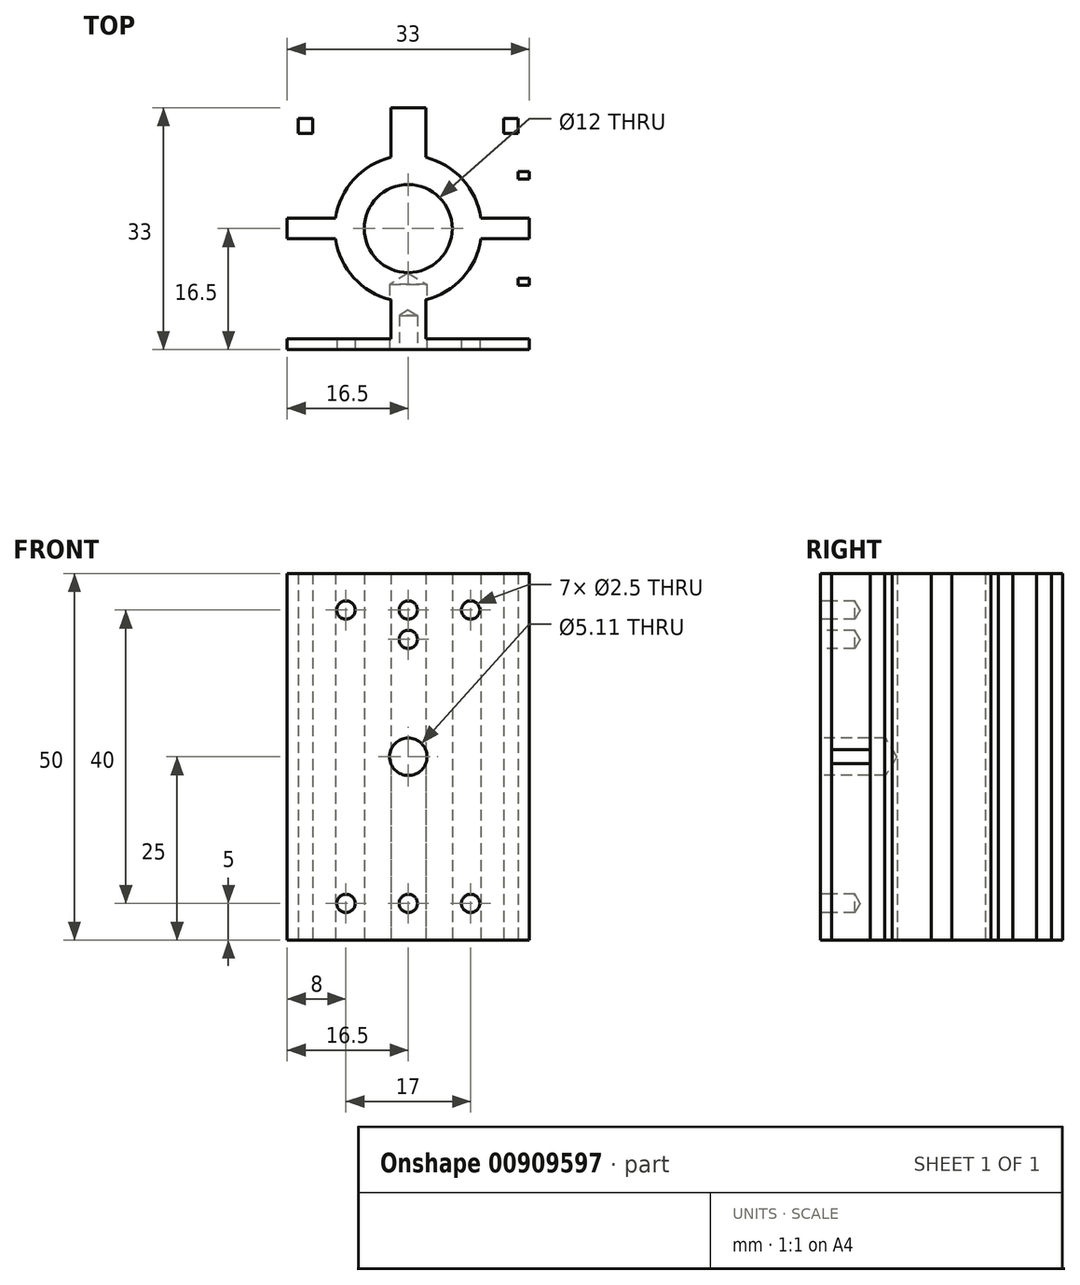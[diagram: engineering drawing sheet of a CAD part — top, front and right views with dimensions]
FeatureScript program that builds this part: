
annotation { "Feature Type Name" : "Feature", "Feature Type Description" : "" }
export const myFeature = defineFeature(function(context is Context, id is Id, definition is map)
    precondition{}
    {
        {
            var Q0;
            Q0=qCreatedBy(makeId("Top.planeOp"),FACE);
            var sketch = newSketch(context, id + "F0", { "sketchPlane" : qUnion([Q0])});
            skLineSegment(sketch, "E0.bottom", {"start": v(16.5, 16.5) * mm, "end": v(-16.5, 16.5) * mm});
            skLineSegment(sketch, "E0.top", {"start": v(16.5, -16.5) * mm, "end": v(-16.5, -16.5) * mm});
            skLineSegment(sketch, "E0.left", {"start": v(16.5, 16.5) * mm, "end": v(16.5, -16.5) * mm});
            skLineSegment(sketch, "E0.right", {"start": v(-16.5, 16.5) * mm, "end": v(-16.5, -16.5) * mm});
            skPoint(sketch, "E0.middle", {"position": v(0, 0) * mm});
            skCircle(sketch, "E1", {"center": v(0, 0) * mm, "radius": 10 * mm});
            skLineSegment(sketch, "E2", {"start": v(0, 16.5) * mm, "end": v(0, -16.5) * mm, "construction": true});
            skLineSegment(sketch, "E3", {"start": v(-16.5, 0) * mm, "end": v(16.5, 0) * mm, "construction": true});
            skLineSegment(sketch, "E4", {"start": v(-2.38, 9.71) * mm, "end": v(-2.38, 16.5) * mm});
            skLineSegment(sketch, "E5.MirrorCS", {"start": v(2.38, 9.71) * mm, "end": v(2.38, 16.5) * mm});
            skLineSegment(sketch, "E6.MirrorCS", {"start": v(-2.38, -9.71) * mm, "end": v(-2.38, -16.5) * mm});
            skLineSegment(sketch, "E7.MirrorCS", {"start": v(2.37, -9.71) * mm, "end": v(2.37, -16.5) * mm});
            skLineSegment(sketch, "E8", {"start": v(-16.5, -1.4) * mm, "end": v(-9.9, -1.4) * mm});
            skLineSegment(sketch, "E9.MirrorCS", {"start": v(-16.5, 1.4) * mm, "end": v(-9.9, 1.4) * mm});
            skLineSegment(sketch, "E10.MirrorCS", {"start": v(16.5, 1.4) * mm, "end": v(9.9, 1.4) * mm});
            skLineSegment(sketch, "E11.MirrorCS", {"start": v(16.5, -1.4) * mm, "end": v(9.9, -1.4) * mm});
            skLineSegment(sketch, "E12.0", {"start": v(13, 13) * mm, "end": v(13, -13) * mm});
            skLineSegment(sketch, "E12.1", {"start": v(13, 13) * mm, "end": v(-13, 13) * mm});
            skLineSegment(sketch, "E12.2", {"start": v(-13, 13) * mm, "end": v(-13, -13) * mm});
            skLineSegment(sketch, "E12.3", {"start": v(13, -13) * mm, "end": v(-13, -13) * mm});
            skLineSegment(sketch, "E13.0", {"start": v(15, 15) * mm, "end": v(-15, 15) * mm});
            skLineSegment(sketch, "E13.1", {"start": v(15, 15) * mm, "end": v(15, -15) * mm});
            skLineSegment(sketch, "E13.2", {"start": v(15, -15) * mm, "end": v(-15, -15) * mm});
            skLineSegment(sketch, "E13.3", {"start": v(-15, 15) * mm, "end": v(-15, -15) * mm});
            skLineSegment(sketch, "E14.bottom", {"start": v(-10.5, 16.5) * mm, "end": v(-9.5, 16.5) * mm});
            skLineSegment(sketch, "E14.top", {"start": v(-10.5, 15) * mm, "end": v(-9.5, 15) * mm});
            skLineSegment(sketch, "E14.left", {"start": v(-10.5, 16.5) * mm, "end": v(-10.5, 15) * mm});
            skLineSegment(sketch, "E14.right", {"start": v(-9.5, 16.5) * mm, "end": v(-9.5, 15) * mm});
            skLineSegment(sketch, "E15.bottom", {"start": v(-16.5, 16.5) * mm, "end": v(-13, 16.5) * mm});
            skLineSegment(sketch, "E15.top", {"start": v(-16.5, 13) * mm, "end": v(-13, 13) * mm});
            skLineSegment(sketch, "E15.left", {"start": v(-16.5, 16.5) * mm, "end": v(-16.5, 13) * mm});
            skLineSegment(sketch, "E15.right", {"start": v(-13, 16.5) * mm, "end": v(-13, 13) * mm});
            skLineSegment(sketch, "E16.1.0.0", {"start": v(-7.75, 16.5) * mm, "end": v(-6.75, 16.5) * mm});
            skLineSegment(sketch, "E16.1.0.1", {"start": v(-7.75, 15) * mm, "end": v(-6.75, 15) * mm});
            skLineSegment(sketch, "E16.1.0.2", {"start": v(-7.75, 16.5) * mm, "end": v(-7.75, 15) * mm});
            skLineSegment(sketch, "E16.1.0.3", {"start": v(-6.75, 16.5) * mm, "end": v(-6.75, 15) * mm});
            skLineSegment(sketch, "E16.2.0.0", {"start": v(-5, 16.5) * mm, "end": v(-4, 16.5) * mm});
            skLineSegment(sketch, "E16.2.0.1", {"start": v(-5, 15) * mm, "end": v(-4, 15) * mm});
            skLineSegment(sketch, "E16.2.0.2", {"start": v(-5, 16.5) * mm, "end": v(-5, 15) * mm});
            skLineSegment(sketch, "E16.2.0.3", {"start": v(-4, 16.5) * mm, "end": v(-4, 15) * mm});
            skLineSegment(sketch, "E16.direction1", {"start": v(-10.5, 15) * mm, "end": v(-7.75, 15) * mm, "construction": true});
            skLineSegment(sketch, "E17.MirrorCS", {"start": v(7.75, 16.5) * mm, "end": v(6.75, 16.5) * mm});
            skLineSegment(sketch, "E18.MirrorCS", {"start": v(7.75, 15) * mm, "end": v(6.75, 15) * mm});
            skLineSegment(sketch, "E19.MirrorCS", {"start": v(10.5, 15) * mm, "end": v(9.5, 15) * mm});
            skLineSegment(sketch, "E20.MirrorCS", {"start": v(7.75, 16.5) * mm, "end": v(7.75, 15) * mm});
            skLineSegment(sketch, "E21.MirrorCS", {"start": v(5, 15) * mm, "end": v(4, 15) * mm});
            skLineSegment(sketch, "E22.MirrorCS", {"start": v(10.5, 16.5) * mm, "end": v(10.5, 15) * mm});
            skLineSegment(sketch, "E23.MirrorCS", {"start": v(4, 16.5) * mm, "end": v(4, 15) * mm});
            skLineSegment(sketch, "E24.MirrorCS", {"start": v(10.5, 16.5) * mm, "end": v(9.5, 16.5) * mm});
            skLineSegment(sketch, "E25.MirrorCS", {"start": v(9.5, 16.5) * mm, "end": v(9.5, 15) * mm});
            skLineSegment(sketch, "E26.MirrorCS", {"start": v(5, 16.5) * mm, "end": v(5, 15) * mm});
            skLineSegment(sketch, "E27.MirrorCS", {"start": v(10.5, 15) * mm, "end": v(7.75, 15) * mm, "construction": true});
            skLineSegment(sketch, "E28.MirrorCS", {"start": v(5, 16.5) * mm, "end": v(4, 16.5) * mm});
            skLineSegment(sketch, "E29.MirrorCS", {"start": v(6.75, 16.5) * mm, "end": v(6.75, 15) * mm});
            skLineSegment(sketch, "E30", {"start": v(16.5, 16.5) * mm, "end": v(-16.5, -16.5) * mm, "construction": true});
            skLineSegment(sketch, "E31.MirrorCS", {"start": v(15, 10.5) * mm, "end": v(15, 9.5) * mm});
            skLineSegment(sketch, "E32.MirrorCS", {"start": v(16.5, 10.5) * mm, "end": v(16.5, 9.5) * mm});
            skLineSegment(sketch, "E33.MirrorCS", {"start": v(16.5, 7.75) * mm, "end": v(15, 7.75) * mm});
            skLineSegment(sketch, "E34.MirrorCS", {"start": v(15, 5) * mm, "end": v(15, 4) * mm});
            skLineSegment(sketch, "E35.MirrorCS", {"start": v(16.5, 4) * mm, "end": v(15, 4) * mm});
            skLineSegment(sketch, "E36.MirrorCS", {"start": v(16.5, 6.75) * mm, "end": v(15, 6.75) * mm});
            skLineSegment(sketch, "E37.MirrorCS", {"start": v(16.5, 7.75) * mm, "end": v(16.5, 6.75) * mm});
            skLineSegment(sketch, "E38.MirrorCS", {"start": v(16.5, 10.5) * mm, "end": v(15, 10.5) * mm});
            skLineSegment(sketch, "E39.MirrorCS", {"start": v(16.5, 5) * mm, "end": v(15, 5) * mm});
            skLineSegment(sketch, "E40.MirrorCS", {"start": v(15, 10.5) * mm, "end": v(15, 7.75) * mm, "construction": true});
            skLineSegment(sketch, "E41.MirrorCS", {"start": v(16.5, 9.5) * mm, "end": v(15, 9.5) * mm});
            skLineSegment(sketch, "E42.MirrorCS", {"start": v(15, 7.75) * mm, "end": v(15, 6.75) * mm});
            skLineSegment(sketch, "E43.MirrorCS", {"start": v(16.5, 5) * mm, "end": v(16.5, 4) * mm});
            skLineSegment(sketch, "E44.MirrorCS", {"start": v(15, -10.5) * mm, "end": v(15, -9.5) * mm});
            skLineSegment(sketch, "E45.MirrorCS", {"start": v(16.5, -7.75) * mm, "end": v(15, -7.75) * mm});
            skLineSegment(sketch, "E46.MirrorCS", {"start": v(16.5, -6.75) * mm, "end": v(15, -6.75) * mm});
            skLineSegment(sketch, "E47.MirrorCS", {"start": v(15, -5) * mm, "end": v(15, -4) * mm});
            skLineSegment(sketch, "E48.MirrorCS", {"start": v(15, -10.5) * mm, "end": v(15, -7.75) * mm, "construction": true});
            skLineSegment(sketch, "E49.MirrorCS", {"start": v(15, -7.75) * mm, "end": v(15, -6.75) * mm});
            skLineSegment(sketch, "E50.MirrorCS", {"start": v(16.5, -7.75) * mm, "end": v(16.5, -6.75) * mm});
            skLineSegment(sketch, "E51.MirrorCS", {"start": v(16.5, -9.5) * mm, "end": v(15, -9.5) * mm});
            skLineSegment(sketch, "E52.MirrorCS", {"start": v(16.5, -5) * mm, "end": v(16.5, -4) * mm});
            skLineSegment(sketch, "E53.MirrorCS", {"start": v(16.5, -4) * mm, "end": v(15, -4) * mm});
            skLineSegment(sketch, "E54.MirrorCS", {"start": v(16.5, -5) * mm, "end": v(15, -5) * mm});
            skLineSegment(sketch, "E55.MirrorCS", {"start": v(16.5, -10.5) * mm, "end": v(16.5, -9.5) * mm});
            skLineSegment(sketch, "E56.MirrorCS", {"start": v(16.5, -10.5) * mm, "end": v(15, -10.5) * mm});
            skLineSegment(sketch, "E57.MirrorCS", {"start": v(-15, 10.5) * mm, "end": v(-15, 9.5) * mm});
            skLineSegment(sketch, "E58.MirrorCS", {"start": v(-15, 7.75) * mm, "end": v(-15, 6.75) * mm});
            skLineSegment(sketch, "E59.MirrorCS", {"start": v(-16.5, 5) * mm, "end": v(-16.5, 4) * mm});
            skLineSegment(sketch, "E60.MirrorCS", {"start": v(-16.5, 4) * mm, "end": v(-15, 4) * mm});
            skLineSegment(sketch, "E61.MirrorCS", {"start": v(-16.5, 7.75) * mm, "end": v(-16.5, 6.75) * mm});
            skLineSegment(sketch, "E62.MirrorCS", {"start": v(-16.5, 5) * mm, "end": v(-15, 5) * mm});
            skLineSegment(sketch, "E63.MirrorCS", {"start": v(-16.5, 9.5) * mm, "end": v(-15, 9.5) * mm});
            skLineSegment(sketch, "E64.MirrorCS", {"start": v(-16.5, 10.5) * mm, "end": v(-16.5, 9.5) * mm});
            skLineSegment(sketch, "E65.MirrorCS", {"start": v(-16.5, 6.75) * mm, "end": v(-15, 6.75) * mm});
            skLineSegment(sketch, "E66.MirrorCS", {"start": v(-16.5, 10.5) * mm, "end": v(-15, 10.5) * mm});
            skLineSegment(sketch, "E67.MirrorCS", {"start": v(-15, 5) * mm, "end": v(-15, 4) * mm});
            skLineSegment(sketch, "E68.MirrorCS", {"start": v(-16.5, 7.75) * mm, "end": v(-15, 7.75) * mm});
            skLineSegment(sketch, "E69.MirrorCS", {"start": v(-15, 10.5) * mm, "end": v(-15, 7.75) * mm, "construction": true});
            skLineSegment(sketch, "E70.MirrorCS", {"start": v(-15, -10.5) * mm, "end": v(-15, -9.5) * mm});
            skLineSegment(sketch, "E71.MirrorCS", {"start": v(-16.5, -5) * mm, "end": v(-16.5, -4) * mm});
            skLineSegment(sketch, "E72.MirrorCS", {"start": v(-15, -7.75) * mm, "end": v(-15, -6.75) * mm});
            skLineSegment(sketch, "E73.MirrorCS", {"start": v(-16.5, -4) * mm, "end": v(-15, -4) * mm});
            skLineSegment(sketch, "E74.MirrorCS", {"start": v(-16.5, -10.5) * mm, "end": v(-16.5, -9.5) * mm});
            skLineSegment(sketch, "E75.MirrorCS", {"start": v(-16.5, -7.75) * mm, "end": v(-15, -7.75) * mm});
            skLineSegment(sketch, "E76.MirrorCS", {"start": v(-16.5, -10.5) * mm, "end": v(-15, -10.5) * mm});
            skLineSegment(sketch, "E77.MirrorCS", {"start": v(-15, -5) * mm, "end": v(-15, -4) * mm});
            skLineSegment(sketch, "E78.MirrorCS", {"start": v(-16.5, -9.5) * mm, "end": v(-15, -9.5) * mm});
            skLineSegment(sketch, "E79.MirrorCS", {"start": v(-16.5, -6.75) * mm, "end": v(-15, -6.75) * mm});
            skLineSegment(sketch, "E80.MirrorCS", {"start": v(-15, -10.5) * mm, "end": v(-15, -7.75) * mm, "construction": true});
            skLineSegment(sketch, "E81.MirrorCS", {"start": v(-16.5, -7.75) * mm, "end": v(-16.5, -6.75) * mm});
            skLineSegment(sketch, "E82.MirrorCS", {"start": v(-16.5, -5) * mm, "end": v(-15, -5) * mm});
            skLineSegment(sketch, "E83.MirrorCS", {"start": v(16.5, 16.5) * mm, "end": v(13, 16.5) * mm});
            skLineSegment(sketch, "E84.MirrorCS", {"start": v(16.5, 16.5) * mm, "end": v(16.5, 13) * mm});
            skLineSegment(sketch, "E85.MirrorCS", {"start": v(16.5, 13) * mm, "end": v(13, 13) * mm});
            skLineSegment(sketch, "E86.MirrorCS", {"start": v(13, 16.5) * mm, "end": v(13, 13) * mm});
            skCircle(sketch, "E87", {"center": v(0, 0) * mm, "radius": 6 * mm});
            skLineSegment(sketch, "E88", {"start": v(-15, -15) * mm, "end": v(-16.5, -15) * mm});
            skLineSegment(sketch, "E89.MirrorCS", {"start": v(15, -15) * mm, "end": v(16.5, -15) * mm});
            skSolve(sketch);
        }
        {
            var Q0;
            Q0=makeQuery(id+"F0.imprint","IMPRINT",FACE,{"disambiguationData":[TD([[makeQuery(id+"F0.imprint","IMPRINT",EDGE,{"derivedFrom":sQuery(id+"F0.wireOp",EDGE,"E14.bottom")}),-1.0]])]});
            var Q1;
            Q1=makeQuery(id+"F0.imprint","IMPRINT",FACE,{"disambiguationData":[TD([[makeQuery(id+"F0.imprint","IMPRINT",EDGE,{"derivedFrom":sQuery(id+"F0.wireOp",EDGE,"E16.1.0.0")}),-1.0]])]});
            var Q2;
            Q2=makeQuery(id+"F0.imprint","IMPRINT",FACE,{"disambiguationData":[TD([[makeQuery(id+"F0.imprint","IMPRINT",EDGE,{"derivedFrom":sQuery(id+"F0.wireOp",EDGE,"E16.2.0.0")}),-1.0]])]});
            var Q3;
            Q3=makeQuery(id+"F0.imprint","IMPRINT",FACE,{"disambiguationData":[TD([[makeQuery(id+"F0.imprint","IMPRINT",EDGE,{"derivedFrom":sQuery(id+"F0.wireOp",EDGE,"E21.MirrorCS")}),-1.0]])]});
            var Q4;
            Q4=makeQuery(id+"F0.imprint","IMPRINT",FACE,{"disambiguationData":[TD([[makeQuery(id+"F0.imprint","IMPRINT",EDGE,{"derivedFrom":sQuery(id+"F0.wireOp",EDGE,"E17.MirrorCS")}),1.0]])]});
            var Q5;
            Q5=makeQuery(id+"F0.imprint","IMPRINT",FACE,{"disambiguationData":[TD([[makeQuery(id+"F0.imprint","IMPRINT",EDGE,{"derivedFrom":sQuery(id+"F0.wireOp",EDGE,"E19.MirrorCS")}),-1.0]])]});
            var Q6;
            {var subQ1=sQuery(id+"F0.wireOp",EDGE,"E83.MirrorCS");Q6=makeQuery(id+"F0.imprint","IMPRINT",FACE,{"disambiguationData":[TD([[makeQuery(id+"F0.imprint","IMPRINT",EDGE,{"derivedFrom":subQ1}),1.0]])]});}
            var Q7;
            {var subQ0=sQuery(id+"F0.wireOp",EDGE,"E13.1");var subQ1=sQuery(id+"F0.wireOp",EDGE,"E13.0");var subQ2=makeQuery(id+"F0.imprint","INTERSECT",VERTEX,{"derivedFrom":[subQ1,subQ0]});Q7=makeQuery(id+"F0.imprint","IMPRINT",FACE,{"disambiguationData":[TD([[makeQuery(id+"F0.imprint","IMPRINT",EDGE,{"disambiguationData":[TD([[subQ2,-1.0]])],"derivedFrom":subQ1}),1.0]])]});}
            var Q8;
            {var subQ0=sQuery(id+"F0.wireOp",EDGE,"E18.MirrorCS");Q8=makeQuery(id+"F0.imprint","IMPRINT",FACE,{"disambiguationData":[TD([[makeQuery(id+"F0.imprint","IMPRINT",EDGE,{"derivedFrom":subQ0}),1.0]])]});}
            var Q9;
            {var subQ0=sQuery(id+"F0.wireOp",EDGE,"E12.1");var subQ1=sQuery(id+"F0.wireOp",EDGE,"E4");var subQ2=makeQuery(id+"F0.imprint","INTERSECT",VERTEX,{"derivedFrom":[subQ1,subQ0]});Q9=makeQuery(id+"F0.imprint","IMPRINT",FACE,{"disambiguationData":[TD([[makeQuery(id+"F0.imprint","IMPRINT",EDGE,{"disambiguationData":[TD([[subQ2,-1.0]])],"derivedFrom":subQ1}),-1.0]])]});}
            var Q10;
            {var subQ0=sQuery(id+"F0.wireOp",EDGE,"E4");var subQ1=sQuery(id+"F0.wireOp",EDGE,"E0.bottom");var subQ2=makeQuery(id+"F0.imprint","INTERSECT",VERTEX,{"derivedFrom":[subQ1,subQ0]});Q10=makeQuery(id+"F0.imprint","IMPRINT",FACE,{"disambiguationData":[TD([[makeQuery(id+"F0.imprint","IMPRINT",EDGE,{"disambiguationData":[TD([[subQ2,1.0]])],"derivedFrom":subQ1}),1.0]])]});}
            var Q11;
            {var subQ9=sQuery(id+"F0.wireOp",EDGE,"E14.top");Q11=makeQuery(id+"F0.imprint","IMPRINT",FACE,{"disambiguationData":[TD([[makeQuery(id+"F0.imprint","IMPRINT",EDGE,{"derivedFrom":subQ9}),-1.0]])]});}
            var Q12;
            {var subQ0=sQuery(id+"F0.wireOp",EDGE,"E13.3");var subQ1=sQuery(id+"F0.wireOp",EDGE,"E13.0");var subQ2=makeQuery(id+"F0.imprint","INTERSECT",VERTEX,{"derivedFrom":[subQ1,subQ0]});Q12=makeQuery(id+"F0.imprint","IMPRINT",FACE,{"disambiguationData":[TD([[makeQuery(id+"F0.imprint","IMPRINT",EDGE,{"disambiguationData":[TD([[subQ2,1.0]])],"derivedFrom":subQ1}),1.0]])]});}
            var Q13;
            {var subQ0=sQuery(id+"F0.wireOp",EDGE,"E15.bottom");Q13=makeQuery(id+"F0.imprint","IMPRINT",FACE,{"disambiguationData":[TD([[makeQuery(id+"F0.imprint","IMPRINT",EDGE,{"derivedFrom":subQ0}),-1.0]])]});}
            var Q14;
            {var subQ0=sQuery(id+"F0.wireOp",EDGE,"E57.MirrorCS");Q14=makeQuery(id+"F0.imprint","IMPRINT",FACE,{"disambiguationData":[TD([[makeQuery(id+"F0.imprint","IMPRINT",EDGE,{"derivedFrom":subQ0}),1.0]])]});}
            var Q15;
            Q15=makeQuery(id+"F0.imprint","IMPRINT",FACE,{"disambiguationData":[TD([[makeQuery(id+"F0.imprint","IMPRINT",EDGE,{"derivedFrom":sQuery(id+"F0.wireOp",EDGE,"E57.MirrorCS")}),-1.0]])]});
            var Q16;
            Q16=makeQuery(id+"F0.imprint","IMPRINT",FACE,{"disambiguationData":[TD([[makeQuery(id+"F0.imprint","IMPRINT",EDGE,{"derivedFrom":sQuery(id+"F0.wireOp",EDGE,"E58.MirrorCS")}),-1.0]])]});
            var Q17;
            Q17=makeQuery(id+"F0.imprint","IMPRINT",FACE,{"disambiguationData":[TD([[makeQuery(id+"F0.imprint","IMPRINT",EDGE,{"derivedFrom":sQuery(id+"F0.wireOp",EDGE,"E59.MirrorCS")}),1.0]])]});
            var Q18;
            {var subQ0=sQuery(id+"F0.wireOp",EDGE,"E8");var subQ1=sQuery(id+"F0.wireOp",EDGE,"E0.right");var subQ2=makeQuery(id+"F0.imprint","INTERSECT",VERTEX,{"derivedFrom":[subQ1,subQ0]});Q18=makeQuery(id+"F0.imprint","IMPRINT",FACE,{"disambiguationData":[TD([[makeQuery(id+"F0.imprint","IMPRINT",EDGE,{"disambiguationData":[TD([[subQ2,1.0]])],"derivedFrom":subQ1}),1.0]])]});}
            var Q19;
            Q19=makeQuery(id+"F0.imprint","IMPRINT",FACE,{"disambiguationData":[TD([[makeQuery(id+"F0.imprint","IMPRINT",EDGE,{"derivedFrom":sQuery(id+"F0.wireOp",EDGE,"E71.MirrorCS")}),-1.0]])]});
            var Q20;
            Q20=makeQuery(id+"F0.imprint","IMPRINT",FACE,{"disambiguationData":[TD([[makeQuery(id+"F0.imprint","IMPRINT",EDGE,{"derivedFrom":sQuery(id+"F0.wireOp",EDGE,"E72.MirrorCS")}),1.0]])]});
            var Q21;
            Q21=makeQuery(id+"F0.imprint","IMPRINT",FACE,{"disambiguationData":[TD([[makeQuery(id+"F0.imprint","IMPRINT",EDGE,{"derivedFrom":sQuery(id+"F0.wireOp",EDGE,"E70.MirrorCS")}),1.0]])]});
            var Q22;
            {var subQ3=sQuery(id+"F0.wireOp",EDGE,"E70.MirrorCS");Q22=makeQuery(id+"F0.imprint","IMPRINT",FACE,{"disambiguationData":[TD([[makeQuery(id+"F0.imprint","IMPRINT",EDGE,{"derivedFrom":subQ3}),-1.0]])]});}
            var Q23;
            {var subQ0=sQuery(id+"F0.wireOp",EDGE,"E13.3");var subQ1=sQuery(id+"F0.wireOp",EDGE,"E8");var subQ2=makeQuery(id+"F0.imprint","INTERSECT",VERTEX,{"derivedFrom":[subQ1,subQ0]});Q23=makeQuery(id+"F0.imprint","IMPRINT",FACE,{"disambiguationData":[TD([[makeQuery(id+"F0.imprint","IMPRINT",EDGE,{"disambiguationData":[TD([[subQ2,-1.0]])],"derivedFrom":subQ1}),1.0]])]});}
            var Q24;
            {var subQ0=sQuery(id+"F0.wireOp",EDGE,"E8");var subQ1=sQuery(id+"F0.wireOp",EDGE,"E1");var subQ2=makeQuery(id+"F0.imprint","INTERSECT",VERTEX,{"derivedFrom":[subQ1,subQ0]});Q24=makeQuery(id+"F0.imprint","IMPRINT",FACE,{"disambiguationData":[TD([[makeQuery(id+"F0.imprint","IMPRINT",EDGE,{"disambiguationData":[TD([[subQ2,1.0]])],"derivedFrom":subQ1}),-1.0]])]});}
            var Q25;
            {var subQ0=sQuery(id+"F0.wireOp",EDGE,"E4");var subQ1=sQuery(id+"F0.wireOp",EDGE,"E1");var subQ2=makeQuery(id+"F0.imprint","INTERSECT",VERTEX,{"derivedFrom":[subQ1,subQ0]});Q25=makeQuery(id+"F0.imprint","IMPRINT",FACE,{"disambiguationData":[TD([[makeQuery(id+"F0.imprint","IMPRINT",EDGE,{"disambiguationData":[TD([[subQ2,1.0]])],"derivedFrom":subQ1}),-1.0]])]});}
            var Q26;
            {var subQ0=sQuery(id+"F0.wireOp",EDGE,"E10.MirrorCS");var subQ1=sQuery(id+"F0.wireOp",EDGE,"E1");var subQ2=makeQuery(id+"F0.imprint","INTERSECT",VERTEX,{"derivedFrom":[subQ1,subQ0]});Q26=makeQuery(id+"F0.imprint","IMPRINT",FACE,{"disambiguationData":[TD([[makeQuery(id+"F0.imprint","IMPRINT",EDGE,{"disambiguationData":[TD([[subQ2,1.0]])],"derivedFrom":subQ1}),-1.0]])]});}
            var Q27;
            {var subQ0=sQuery(id+"F0.wireOp",EDGE,"E13.1");var subQ1=sQuery(id+"F0.wireOp",EDGE,"E10.MirrorCS");var subQ2=makeQuery(id+"F0.imprint","INTERSECT",VERTEX,{"derivedFrom":[subQ1,subQ0]});Q27=makeQuery(id+"F0.imprint","IMPRINT",FACE,{"disambiguationData":[TD([[makeQuery(id+"F0.imprint","IMPRINT",EDGE,{"disambiguationData":[TD([[subQ2,-1.0]])],"derivedFrom":subQ1}),1.0]])]});}
            var Q28;
            Q28=makeQuery(id+"F0.imprint","IMPRINT",FACE,{"disambiguationData":[TD([[makeQuery(id+"F0.imprint","IMPRINT",EDGE,{"derivedFrom":sQuery(id+"F0.wireOp",EDGE,"E31.MirrorCS")}),1.0]])]});
            var Q29;
            Q29=makeQuery(id+"F0.imprint","IMPRINT",FACE,{"disambiguationData":[TD([[makeQuery(id+"F0.imprint","IMPRINT",EDGE,{"derivedFrom":sQuery(id+"F0.wireOp",EDGE,"E33.MirrorCS")}),1.0]])]});
            var Q30;
            Q30=makeQuery(id+"F0.imprint","IMPRINT",FACE,{"disambiguationData":[TD([[makeQuery(id+"F0.imprint","IMPRINT",EDGE,{"derivedFrom":sQuery(id+"F0.wireOp",EDGE,"E34.MirrorCS")}),1.0]])]});
            var Q31;
            {var subQ0=sQuery(id+"F0.wireOp",EDGE,"E10.MirrorCS");var subQ1=sQuery(id+"F0.wireOp",EDGE,"E0.left");var subQ2=makeQuery(id+"F0.imprint","INTERSECT",VERTEX,{"derivedFrom":[subQ1,subQ0]});Q31=makeQuery(id+"F0.imprint","IMPRINT",FACE,{"disambiguationData":[TD([[makeQuery(id+"F0.imprint","IMPRINT",EDGE,{"disambiguationData":[TD([[subQ2,-1.0]])],"derivedFrom":subQ1}),-1.0]])]});}
            var Q32;
            {var subQ0=sQuery(id+"F0.wireOp",EDGE,"E31.MirrorCS");Q32=makeQuery(id+"F0.imprint","IMPRINT",FACE,{"disambiguationData":[TD([[makeQuery(id+"F0.imprint","IMPRINT",EDGE,{"derivedFrom":subQ0}),-1.0]])]});}
            var Q33;
            {var subQ0=sQuery(id+"F0.wireOp",EDGE,"E44.MirrorCS");Q33=makeQuery(id+"F0.imprint","IMPRINT",FACE,{"disambiguationData":[TD([[makeQuery(id+"F0.imprint","IMPRINT",EDGE,{"derivedFrom":subQ0}),1.0]])]});}
            var Q34;
            Q34=makeQuery(id+"F0.imprint","IMPRINT",FACE,{"disambiguationData":[TD([[makeQuery(id+"F0.imprint","IMPRINT",EDGE,{"derivedFrom":sQuery(id+"F0.wireOp",EDGE,"E47.MirrorCS")}),-1.0]])]});
            var Q35;
            Q35=makeQuery(id+"F0.imprint","IMPRINT",FACE,{"disambiguationData":[TD([[makeQuery(id+"F0.imprint","IMPRINT",EDGE,{"derivedFrom":sQuery(id+"F0.wireOp",EDGE,"E45.MirrorCS")}),-1.0]])]});
            var Q36;
            Q36=makeQuery(id+"F0.imprint","IMPRINT",FACE,{"disambiguationData":[TD([[makeQuery(id+"F0.imprint","IMPRINT",EDGE,{"derivedFrom":sQuery(id+"F0.wireOp",EDGE,"E44.MirrorCS")}),-1.0]])]});
            var Q37;
            {var subQ0=sQuery(id+"F0.wireOp",EDGE,"E12.3");var subQ1=sQuery(id+"F0.wireOp",EDGE,"E6.MirrorCS");var subQ2=makeQuery(id+"F0.imprint","INTERSECT",VERTEX,{"derivedFrom":[subQ1,subQ0]});Q37=makeQuery(id+"F0.imprint","IMPRINT",FACE,{"disambiguationData":[TD([[makeQuery(id+"F0.imprint","IMPRINT",EDGE,{"disambiguationData":[TD([[subQ2,-1.0]])],"derivedFrom":subQ1}),1.0]])]});}
            var Q38;
            {var subQ0=sQuery(id+"F0.wireOp",EDGE,"E6.MirrorCS");var subQ1=sQuery(id+"F0.wireOp",EDGE,"E0.top");var subQ2=makeQuery(id+"F0.imprint","INTERSECT",VERTEX,{"derivedFrom":[subQ1,subQ0]});Q38=makeQuery(id+"F0.imprint","IMPRINT",FACE,{"disambiguationData":[TD([[makeQuery(id+"F0.imprint","IMPRINT",EDGE,{"disambiguationData":[TD([[subQ2,1.0]])],"derivedFrom":subQ1}),-1.0]])]});}
            var Q39;
            {var subQ0=sQuery(id+"F0.wireOp",EDGE,"E89.MirrorCS");Q39=makeQuery(id+"F0.imprint","IMPRINT",FACE,{"disambiguationData":[TD([[makeQuery(id+"F0.imprint","IMPRINT",EDGE,{"derivedFrom":subQ0}),-1.0]])]});}
            var Q40;
            {var subQ0=sQuery(id+"F0.wireOp",EDGE,"E88");Q40=makeQuery(id+"F0.imprint","IMPRINT",FACE,{"disambiguationData":[TD([[makeQuery(id+"F0.imprint","IMPRINT",EDGE,{"derivedFrom":subQ0}),1.0]])]});}
            var Q41;
            {var subQ0=sQuery(id+"F0.wireOp",EDGE,"E6.MirrorCS");var subQ1=sQuery(id+"F0.wireOp",EDGE,"E1");var subQ2=makeQuery(id+"F0.imprint","INTERSECT",VERTEX,{"derivedFrom":[subQ1,subQ0]});Q41=makeQuery(id+"F0.imprint","IMPRINT",FACE,{"disambiguationData":[TD([[makeQuery(id+"F0.imprint","IMPRINT",EDGE,{"disambiguationData":[TD([[subQ2,-1.0]])],"derivedFrom":subQ1}),-1.0]])]});}
            var Q42;
            Q42=makeQuery(id+"F0.imprint","IMPRINT",FACE,{"disambiguationData":[TD([[makeQuery(id+"F0.imprint","IMPRINT",EDGE,{"derivedFrom":sQuery(id+"F0.wireOp",EDGE,"E87")}),-1.0]])]});
            extrude(context, id + "F1", {"entities" : qUnion([Q0, Q1, Q2, Q3, Q4, Q5, Q6, Q7, Q8, Q9, Q10, Q11, Q12, Q13, Q14, Q15, Q16, Q17, Q18, Q19, Q20, Q21, Q22, Q23, Q24, Q25, Q26, Q27, Q28, Q29, Q30, Q31, Q32, Q33, Q34, Q35, Q36, Q37, Q38, Q39, Q40, Q41, Q42]), "depth" : 50 * mm, "offsetDistance" : 25.4 * mm});
        }
        {
            var Q0;
            Q0=makeQuery(id+"F1.opExtrude","SWEPT_FACE",FACE,{"disambiguationData":[OSD([sQuery(id+"F0.wireOp",EDGE,"E0.top")])]});
            var sketch = newSketch(context, id + "F2", { "sketchPlane" : qUnion([Q0])});
            skCircle(sketch, "E90", {"center": v(0, 25) * mm, "radius": 2.55 * mm});
            skPoint(sketch, "E90.centerSnap0", {"position": v(16.5, 25) * mm});
            skPoint(sketch, "E90.centerSnap1", {"position": v(0, 50) * mm});
            skCircle(sketch, "E91", {"center": v(0, 45) * mm, "radius": 1.25 * mm});
            skCircle(sketch, "E92", {"center": v(-8.5, 45) * mm, "radius": 1.25 * mm});
            skLineSegment(sketch, "E93", {"start": v(-16.5, 25) * mm, "end": v(16.5, 25) * mm, "construction": true});
            skLineSegment(sketch, "E94", {"start": v(0, 0) * mm, "end": v(0, 50) * mm, "construction": true});
            skCircle(sketch, "E95.MirrorC", {"center": v(8.5, 45) * mm, "radius": 1.25 * mm});
            skCircle(sketch, "E96.MirrorC", {"center": v(-8.5, 5) * mm, "radius": 1.25 * mm});
            skCircle(sketch, "E97.MirrorC", {"center": v(8.5, 5) * mm, "radius": 1.25 * mm});
            skCircle(sketch, "E98.MirrorC", {"center": v(0, 5) * mm, "radius": 1.25 * mm});
            skCircle(sketch, "E99", {"center": v(0, 41) * mm, "radius": 1.25 * mm});
            skSolve(sketch);
        }
        {
            var Q0;
            Q0=sQuery(id+"F2.wireOp",VERTEX,"E90.center");
            var Q1;
            Q1=makeQuery(id+"F1.opExtrude","SWEPT_BODY",BODY,{"disambiguationData":[OSD([sQuery(id+"F0.wireOp",EDGE,"E0.bottom"),sQuery(id+"F0.wireOp",EDGE,"E0.top"),sQuery(id+"F0.wireOp",EDGE,"E0.left"),sQuery(id+"F0.wireOp",EDGE,"E0.right"),sQuery(id+"F0.wireOp",EDGE,"E1"),sQuery(id+"F0.wireOp",EDGE,"E4"),sQuery(id+"F0.wireOp",EDGE,"E5.MirrorCS"),sQuery(id+"F0.wireOp",EDGE,"E6.MirrorCS"),sQuery(id+"F0.wireOp",EDGE,"E7.MirrorCS"),sQuery(id+"F0.wireOp",EDGE,"E8"),sQuery(id+"F0.wireOp",EDGE,"E9.MirrorCS"),sQuery(id+"F0.wireOp",EDGE,"E10.MirrorCS"),sQuery(id+"F0.wireOp",EDGE,"E11.MirrorCS"),sQuery(id+"F0.wireOp",EDGE,"E12.0"),sQuery(id+"F0.wireOp",EDGE,"E12.1"),sQuery(id+"F0.wireOp",EDGE,"E12.2"),sQuery(id+"F0.wireOp",EDGE,"E12.3"),sQuery(id+"F0.wireOp",EDGE,"E13.0"),sQuery(id+"F0.wireOp",EDGE,"E13.1"),sQuery(id+"F0.wireOp",EDGE,"E13.3"),sQuery(id+"F0.wireOp",EDGE,"E14.bottom"),sQuery(id+"F0.wireOp",EDGE,"E14.left"),sQuery(id+"F0.wireOp",EDGE,"E14.right"),sQuery(id+"F0.wireOp",EDGE,"E15.bottom"),sQuery(id+"F0.wireOp",EDGE,"E15.top"),sQuery(id+"F0.wireOp",EDGE,"E15.left"),sQuery(id+"F0.wireOp",EDGE,"E15.right"),sQuery(id+"F0.wireOp",EDGE,"E16.1.0.0"),sQuery(id+"F0.wireOp",EDGE,"E16.1.0.2"),sQuery(id+"F0.wireOp",EDGE,"E16.1.0.3"),sQuery(id+"F0.wireOp",EDGE,"E16.2.0.0"),sQuery(id+"F0.wireOp",EDGE,"E16.2.0.2"),sQuery(id+"F0.wireOp",EDGE,"E16.2.0.3"),sQuery(id+"F0.wireOp",EDGE,"E17.MirrorCS"),sQuery(id+"F0.wireOp",EDGE,"E20.MirrorCS"),sQuery(id+"F0.wireOp",EDGE,"E22.MirrorCS"),sQuery(id+"F0.wireOp",EDGE,"E23.MirrorCS"),sQuery(id+"F0.wireOp",EDGE,"E24.MirrorCS"),sQuery(id+"F0.wireOp",EDGE,"E25.MirrorCS"),sQuery(id+"F0.wireOp",EDGE,"E26.MirrorCS"),sQuery(id+"F0.wireOp",EDGE,"E28.MirrorCS"),sQuery(id+"F0.wireOp",EDGE,"E29.MirrorCS"),sQuery(id+"F0.wireOp",EDGE,"E32.MirrorCS"),sQuery(id+"F0.wireOp",EDGE,"E33.MirrorCS"),sQuery(id+"F0.wireOp",EDGE,"E35.MirrorCS"),sQuery(id+"F0.wireOp",EDGE,"E36.MirrorCS"),sQuery(id+"F0.wireOp",EDGE,"E37.MirrorCS"),sQuery(id+"F0.wireOp",EDGE,"E38.MirrorCS"),sQuery(id+"F0.wireOp",EDGE,"E39.MirrorCS"),sQuery(id+"F0.wireOp",EDGE,"E41.MirrorCS"),sQuery(id+"F0.wireOp",EDGE,"E43.MirrorCS"),sQuery(id+"F0.wireOp",EDGE,"E45.MirrorCS"),sQuery(id+"F0.wireOp",EDGE,"E46.MirrorCS"),sQuery(id+"F0.wireOp",EDGE,"E50.MirrorCS"),sQuery(id+"F0.wireOp",EDGE,"E51.MirrorCS"),sQuery(id+"F0.wireOp",EDGE,"E52.MirrorCS"),sQuery(id+"F0.wireOp",EDGE,"E53.MirrorCS"),sQuery(id+"F0.wireOp",EDGE,"E54.MirrorCS"),sQuery(id+"F0.wireOp",EDGE,"E55.MirrorCS"),sQuery(id+"F0.wireOp",EDGE,"E56.MirrorCS"),sQuery(id+"F0.wireOp",EDGE,"E59.MirrorCS"),sQuery(id+"F0.wireOp",EDGE,"E60.MirrorCS"),sQuery(id+"F0.wireOp",EDGE,"E61.MirrorCS"),sQuery(id+"F0.wireOp",EDGE,"E62.MirrorCS"),sQuery(id+"F0.wireOp",EDGE,"E63.MirrorCS"),sQuery(id+"F0.wireOp",EDGE,"E64.MirrorCS"),sQuery(id+"F0.wireOp",EDGE,"E65.MirrorCS"),sQuery(id+"F0.wireOp",EDGE,"E66.MirrorCS"),sQuery(id+"F0.wireOp",EDGE,"E68.MirrorCS"),sQuery(id+"F0.wireOp",EDGE,"E71.MirrorCS"),sQuery(id+"F0.wireOp",EDGE,"E73.MirrorCS"),sQuery(id+"F0.wireOp",EDGE,"E74.MirrorCS"),sQuery(id+"F0.wireOp",EDGE,"E75.MirrorCS"),sQuery(id+"F0.wireOp",EDGE,"E76.MirrorCS"),sQuery(id+"F0.wireOp",EDGE,"E78.MirrorCS"),sQuery(id+"F0.wireOp",EDGE,"E79.MirrorCS"),sQuery(id+"F0.wireOp",EDGE,"E81.MirrorCS"),sQuery(id+"F0.wireOp",EDGE,"E82.MirrorCS"),sQuery(id+"F0.wireOp",EDGE,"E83.MirrorCS"),sQuery(id+"F0.wireOp",EDGE,"E84.MirrorCS"),sQuery(id+"F0.wireOp",EDGE,"E85.MirrorCS"),sQuery(id+"F0.wireOp",EDGE,"E86.MirrorCS"),sQuery(id+"F0.wireOp",EDGE,"E87"),sQuery(id+"F0.wireOp",EDGE,"E88"),sQuery(id+"F0.wireOp",EDGE,"E89.MirrorCS")])]});
            hole(context, id + "F3", {"style" : HoleStyle.SIMPLE, "endStyle" : HoleEndStyle.BLIND, "standardTappedOrClearance" : lookupTablePath({ "standard" : "ANSI", "engagement" : "75%", "pitch" : "20 tpi", "size" : "1/4", "type" : "Tapped" }), "standardBlindInLast" : lookupTablePath({ "standard" : "ANSI", "engagement" : "75%", "pitch" : "20 tpi", "size" : "1/4", "type" : "Tapped" }), "holeDiameter" : 5.1 * mm, "majorDiameter" : 6.35 * mm, "showTappedDepth" : true, "holeDepth" : 8.9 * mm, "isTappedThrough" : true, "tappedDepth" : 5.08 * mm, "tapClearance" : 3, "locations" : qUnion([Q0]), "scope" : qUnion([Q1])});
        }
        {
            var Q0;
            Q0=sQuery(id+"F2.wireOp",VERTEX,"E92.center");
            var Q1;
            Q1=sQuery(id+"F2.wireOp",VERTEX,"E91.center");
            var Q2;
            Q2=sQuery(id+"F2.wireOp",VERTEX,"E99.center");
            var Q3;
            Q3=sQuery(id+"F2.wireOp",VERTEX,"E95.MirrorC.center");
            var Q4;
            Q4=sQuery(id+"F2.wireOp",VERTEX,"E97.MirrorC.center");
            var Q5;
            Q5=sQuery(id+"F2.wireOp",VERTEX,"E98.MirrorC.center");
            var Q6;
            Q6=sQuery(id+"F2.wireOp",VERTEX,"E96.MirrorC.center");
            var Q7;
            Q7=makeQuery(id+"F1.opExtrude","SWEPT_BODY",BODY,{"disambiguationData":[OSD([sQuery(id+"F0.wireOp",EDGE,"E0.bottom"),sQuery(id+"F0.wireOp",EDGE,"E0.top"),sQuery(id+"F0.wireOp",EDGE,"E0.left"),sQuery(id+"F0.wireOp",EDGE,"E0.right"),sQuery(id+"F0.wireOp",EDGE,"E1"),sQuery(id+"F0.wireOp",EDGE,"E4"),sQuery(id+"F0.wireOp",EDGE,"E5.MirrorCS"),sQuery(id+"F0.wireOp",EDGE,"E6.MirrorCS"),sQuery(id+"F0.wireOp",EDGE,"E7.MirrorCS"),sQuery(id+"F0.wireOp",EDGE,"E8"),sQuery(id+"F0.wireOp",EDGE,"E9.MirrorCS"),sQuery(id+"F0.wireOp",EDGE,"E10.MirrorCS"),sQuery(id+"F0.wireOp",EDGE,"E11.MirrorCS"),sQuery(id+"F0.wireOp",EDGE,"E12.0"),sQuery(id+"F0.wireOp",EDGE,"E12.1"),sQuery(id+"F0.wireOp",EDGE,"E12.2"),sQuery(id+"F0.wireOp",EDGE,"E12.3"),sQuery(id+"F0.wireOp",EDGE,"E13.0"),sQuery(id+"F0.wireOp",EDGE,"E13.1"),sQuery(id+"F0.wireOp",EDGE,"E13.3"),sQuery(id+"F0.wireOp",EDGE,"E14.bottom"),sQuery(id+"F0.wireOp",EDGE,"E14.left"),sQuery(id+"F0.wireOp",EDGE,"E14.right"),sQuery(id+"F0.wireOp",EDGE,"E15.bottom"),sQuery(id+"F0.wireOp",EDGE,"E15.top"),sQuery(id+"F0.wireOp",EDGE,"E15.left"),sQuery(id+"F0.wireOp",EDGE,"E15.right"),sQuery(id+"F0.wireOp",EDGE,"E16.1.0.0"),sQuery(id+"F0.wireOp",EDGE,"E16.1.0.2"),sQuery(id+"F0.wireOp",EDGE,"E16.1.0.3"),sQuery(id+"F0.wireOp",EDGE,"E16.2.0.0"),sQuery(id+"F0.wireOp",EDGE,"E16.2.0.2"),sQuery(id+"F0.wireOp",EDGE,"E16.2.0.3"),sQuery(id+"F0.wireOp",EDGE,"E17.MirrorCS"),sQuery(id+"F0.wireOp",EDGE,"E20.MirrorCS"),sQuery(id+"F0.wireOp",EDGE,"E22.MirrorCS"),sQuery(id+"F0.wireOp",EDGE,"E23.MirrorCS"),sQuery(id+"F0.wireOp",EDGE,"E24.MirrorCS"),sQuery(id+"F0.wireOp",EDGE,"E25.MirrorCS"),sQuery(id+"F0.wireOp",EDGE,"E26.MirrorCS"),sQuery(id+"F0.wireOp",EDGE,"E28.MirrorCS"),sQuery(id+"F0.wireOp",EDGE,"E29.MirrorCS"),sQuery(id+"F0.wireOp",EDGE,"E32.MirrorCS"),sQuery(id+"F0.wireOp",EDGE,"E33.MirrorCS"),sQuery(id+"F0.wireOp",EDGE,"E35.MirrorCS"),sQuery(id+"F0.wireOp",EDGE,"E36.MirrorCS"),sQuery(id+"F0.wireOp",EDGE,"E37.MirrorCS"),sQuery(id+"F0.wireOp",EDGE,"E38.MirrorCS"),sQuery(id+"F0.wireOp",EDGE,"E39.MirrorCS"),sQuery(id+"F0.wireOp",EDGE,"E41.MirrorCS"),sQuery(id+"F0.wireOp",EDGE,"E43.MirrorCS"),sQuery(id+"F0.wireOp",EDGE,"E45.MirrorCS"),sQuery(id+"F0.wireOp",EDGE,"E46.MirrorCS"),sQuery(id+"F0.wireOp",EDGE,"E50.MirrorCS"),sQuery(id+"F0.wireOp",EDGE,"E51.MirrorCS"),sQuery(id+"F0.wireOp",EDGE,"E52.MirrorCS"),sQuery(id+"F0.wireOp",EDGE,"E53.MirrorCS"),sQuery(id+"F0.wireOp",EDGE,"E54.MirrorCS"),sQuery(id+"F0.wireOp",EDGE,"E55.MirrorCS"),sQuery(id+"F0.wireOp",EDGE,"E56.MirrorCS"),sQuery(id+"F0.wireOp",EDGE,"E59.MirrorCS"),sQuery(id+"F0.wireOp",EDGE,"E60.MirrorCS"),sQuery(id+"F0.wireOp",EDGE,"E61.MirrorCS"),sQuery(id+"F0.wireOp",EDGE,"E62.MirrorCS"),sQuery(id+"F0.wireOp",EDGE,"E63.MirrorCS"),sQuery(id+"F0.wireOp",EDGE,"E64.MirrorCS"),sQuery(id+"F0.wireOp",EDGE,"E65.MirrorCS"),sQuery(id+"F0.wireOp",EDGE,"E66.MirrorCS"),sQuery(id+"F0.wireOp",EDGE,"E68.MirrorCS"),sQuery(id+"F0.wireOp",EDGE,"E71.MirrorCS"),sQuery(id+"F0.wireOp",EDGE,"E73.MirrorCS"),sQuery(id+"F0.wireOp",EDGE,"E74.MirrorCS"),sQuery(id+"F0.wireOp",EDGE,"E75.MirrorCS"),sQuery(id+"F0.wireOp",EDGE,"E76.MirrorCS"),sQuery(id+"F0.wireOp",EDGE,"E78.MirrorCS"),sQuery(id+"F0.wireOp",EDGE,"E79.MirrorCS"),sQuery(id+"F0.wireOp",EDGE,"E81.MirrorCS"),sQuery(id+"F0.wireOp",EDGE,"E82.MirrorCS"),sQuery(id+"F0.wireOp",EDGE,"E83.MirrorCS"),sQuery(id+"F0.wireOp",EDGE,"E84.MirrorCS"),sQuery(id+"F0.wireOp",EDGE,"E85.MirrorCS"),sQuery(id+"F0.wireOp",EDGE,"E86.MirrorCS"),sQuery(id+"F0.wireOp",EDGE,"E87"),sQuery(id+"F0.wireOp",EDGE,"E88"),sQuery(id+"F0.wireOp",EDGE,"E89.MirrorCS")])]});
            hole(context, id + "F4", {"style" : HoleStyle.SIMPLE, "endStyle" : HoleEndStyle.BLIND, "standardTappedOrClearance" : lookupTablePath({ "standard" : "ISO", "engagement" : "75%", "pitch" : "0.5 mm", "size" : "M3", "type" : "Tapped" }), "standardBlindInLast" : lookupTablePath({ "standard" : "ISO", "engagement" : "75%", "pitch" : "0.5 mm", "size" : "M3", "type" : "Tapped" }), "holeDiameter" : 2.5 * mm, "majorDiameter" : 3 * mm, "showTappedDepth" : true, "holeDepth" : 4.67 * mm, "isTappedThrough" : true, "tappedDepth" : 3.17 * mm, "tapClearance" : 3, "locations" : qUnion([Q0, Q1, Q2, Q3, Q4, Q5, Q6]), "scope" : qUnion([Q7])});
        }
    });
